# Revit family: Window-Casement-Pella-Architect_Series-Half_Circle
name_source: partatom
category: Windows
revit_build: Autodesk Revit Architecture 2013 (Build: 20130531_2115(x64)
units: mm (PartAtom-declared; Revit-internal decimal feet)

## types (7) — shared parameters
Analytic Construction = <None>
Architectural Data Sheet = To be determined
Architectural Design Manual = www.pellaadm.com
Construction Type = -
Custom Arc Radius = No
Custom Grille Pattern = Yes
Default Sill Height = 4' - 0"
Description = Casement Half Circle
Egress Window = No
Energy Efficiency = http://www.pella.com
Environmental Commitment = http://www.pella.com
Ext Finish = Aluminum - Pella - Brown
Glazing Finish = Glass - Pella - Clear Insulating Glass
Glazing Thickness = 0' - 0 5/8"
Grille Visibility = Yes
Heat Transfer Coefficient (U) = 0.1000 BTU/(h·ft²·°F)
Int Finish = Wood - Pella - Pine
Manufacturer = Pella Windows & Doors
Number of Arcs = 4
Operation = Casement
Product Documentation Link = http://media.pella.com
Product Name = Architect Series Half Circle
Product Page URL = http://www.pella.com
Series = Architect Series - Aluminum-Clad Wood
Size Constraints = Window Sizing constraints available in 6.35 mm increments
Thermal Resistance (R) = 10.0000 (h·ft²·°F)/BTU
URL = www.pella.com
Wall Closure = By host
zero-valued in all types: Solar Heat Gain Coefficient, Visual Light Transmittance

## per-type parameters (varying)
| type | Glazing Height | Glazing Width | Head Height | Height | Rough Height | Rough Width | Sash Height | Sash Width | Unit Height | Unit Width | Width |
| 7437 | 2' - 8" | 5' - 8 1/4" | 7' - 1" | 3' - 1" | 3' - 1 3/4" | 6' - 2 3/4" | 2' - 10 1/2" | 5' - 11 1/2" | 3' - 1" | 6' - 2" | 6' - 2" |
| 7538 | 2' - 8 1/2" | 5' - 9 1/4" | 7' - 1 1/2" | 3' - 1 1/2" | 3' - 2 1/4" | 6' - 3 3/4" | 2' - 11" | 6' - 0 1/2" | 3' - 1 1/2" | 6' - 3" | 6' - 3" |
| 8241 | 3' - 0" | 6' - 4 1/4" | 7' - 5" | 3' - 5" | 3' - 5 3/4" | 6' - 10 3/4" | 3' - 2 1/2" | 6' - 7 1/2" | 3' - 5" | 6' - 10" | 6' - 10" |
| 8744 | 3' - 2 1/2" | 6' - 9 1/4" | 7' - 7 1/2" | 3' - 7 1/2" | 3' - 8 1/4" | 7' - 3 3/4" | 3' - 5" | 7' - 0 1/2" | 3' - 7 1/2" | 7' - 3" | 7' - 3" |
| 9045 | 3' - 4" | 7' - 0 1/4" | 7' - 9" | 3' - 9" | 3' - 9 3/4" | 7' - 6 3/4" | 3' - 6 1/2" | 7' - 3 1/2" | 3' - 9" | 7' - 6" | 7' - 6" |
| 9950 | 3' - 8 1/2" | 7' - 9 1/4" | 8' - 1 1/2" | 4' - 1 1/2" | 4' - 2 1/4" | 8' - 3 3/4" | 3' - 11" | 8' - 0 1/2" | 4' - 1 1/2" | 8' - 3" | 8' - 3" |
| 10553 | 3' - 11 1/2" | 8' - 3 1/4" | 8' - 4 1/2" | 4' - 4 1/2" | 4' - 5 1/4" | 8' - 9 3/4" | 4' - 2" | 8' - 6 1/2" | 4' - 4 1/2" | 8' - 9" | 8' - 9" |

note: column(s) folded — value = type name in every type: Model

## geometry (parser evidence)
native form markers: Blend x10, Sweep x6
no freeform markers — native parametric forms only
